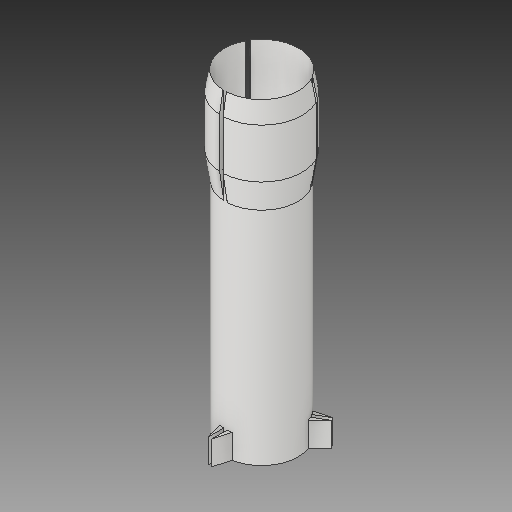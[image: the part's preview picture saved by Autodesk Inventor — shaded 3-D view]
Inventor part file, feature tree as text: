
AUTODESK INVENTOR PART (.ipt)
format: ipt  version: 2017 (Build 210142000, 142)  size: 189,952 bytes
history: native  units: in
note: dims shown in document units (in); Inventor stores cm internally (conversion verified against a paired STEP export)
features: extrude x3, sketch x2, plane x1, revolve x1
ambient origin geometry x8: Origin, YZ Plane, XZ Plane, XY Plane, X Axis, Y Axis, Z Axis, Center Point
bodies: Solid1 (feature_tree)
feature tree (7):
  sketch  "Sketch1"  dims[d0=0.475in d1=3.6in]
  plane  "Work Plane1"
  sketch  "Sketch2"  dims[d10=0.025in d11=0.025in d12=0.025in d13=0.025in d14=0.025in d15=0.025in d24=0.24in d25=0.24in d27=0.24in d28=0.24in d29=0.24in d30=0.35in d31=0.0in d32=4.9125in d33=0.0in d39=0.535in d41=180.0deg d43=90.0deg d44=6.875in d45=0.0in]
  extrude  "Extrusion1"  Depth=3.6in
  extrude  "Extrusion2"  Depth=0.025in
  revolve  "Revolution2"  [1 undecoded]
  extrude  "Extrusion3"  Depth=0.025in
note: 1 required parameter value undecoded (feature->parameter linkage not recoverable at this tier; creation-order binding heuristic only, values carry confidence <= 0.55)
